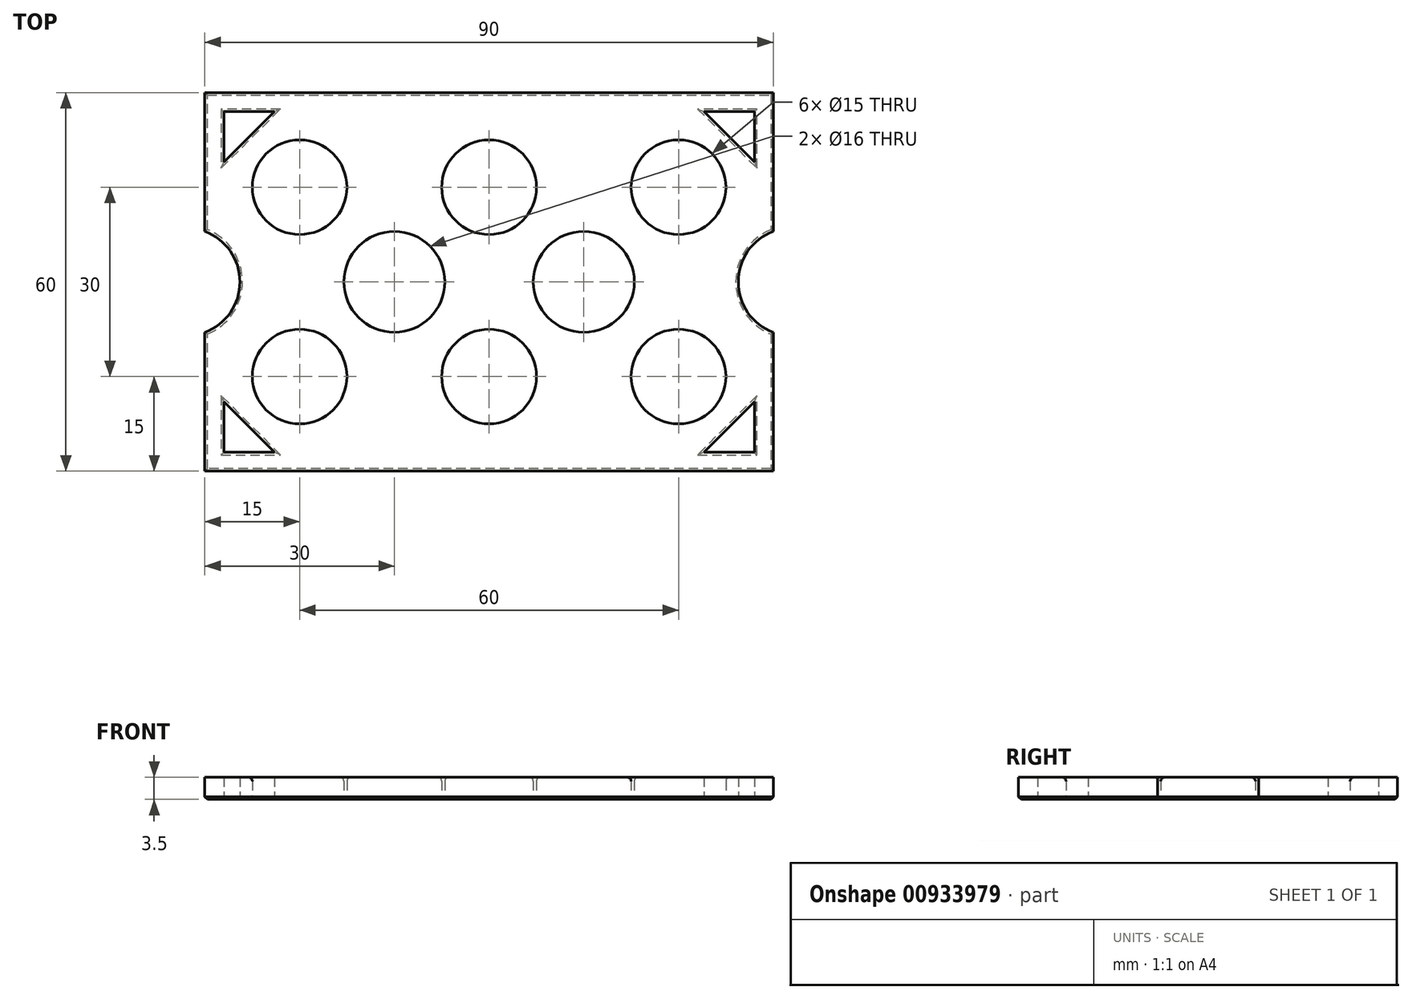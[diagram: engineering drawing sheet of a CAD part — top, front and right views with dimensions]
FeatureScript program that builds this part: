
annotation { "Feature Type Name" : "Feature", "Feature Type Description" : "" }
export const myFeature = defineFeature(function(context is Context, id is Id, definition is map)
    precondition{}
    {
        {
            var Q0;
            Q0=qCreatedBy(makeId("Top.planeOp"),FACE);
            var sketch = newSketch(context, id + "F0", { "sketchPlane" : qUnion([Q0])});
            skLineSegment(sketch, "E0.bottom", {"start": v(-45, 30) * mm, "end": v(45, 30) * mm});
            skLineSegment(sketch, "E0.top", {"start": v(-45, -30) * mm, "end": v(45, -30) * mm});
            skLineSegment(sketch, "E0.left", {"start": v(-45, 30) * mm, "end": v(-45, -30) * mm});
            skLineSegment(sketch, "E0.right", {"start": v(45, 30) * mm, "end": v(45, -30) * mm});
            skPoint(sketch, "E1", {"position": v(45, 0) * mm});
            skPoint(sketch, "E2", {"position": v(0, -30) * mm});
            skSolve(sketch);
        }
        {
            var Q0;
            Q0=qSketchRegion(id+"F0",true);
            extrude(context, id + "F1", {"entities" : qUnion([Q0]), "depth" : 3.5 * mm, "offsetDistance" : 25 * mm});
        }
        {
            var Q0;
            Q0=qCreatedBy(makeId("Top.planeOp"),FACE);
            var sketch = newSketch(context, id + "F2", { "sketchPlane" : qUnion([Q0])});
            skCircle(sketch, "E3", {"center": v(0, 15) * mm, "radius": 7.5 * mm});
            skCircle(sketch, "E4", {"center": v(30, 15) * mm, "radius": 7.5 * mm});
            skCircle(sketch, "E5", {"center": v(15, 0) * mm, "radius": 8 * mm});
            skCircle(sketch, "E6.MirrorC", {"center": v(-30, 15) * mm, "radius": 7.5 * mm});
            skCircle(sketch, "E7.MirrorC", {"center": v(30, -15) * mm, "radius": 7.5 * mm});
            skCircle(sketch, "E8.MirrorC", {"center": v(0, -15) * mm, "radius": 7.5 * mm});
            skCircle(sketch, "E9.MirrorC", {"center": v(-30, -15) * mm, "radius": 7.5 * mm});
            skCircle(sketch, "E10.MirrorC", {"center": v(-15, 0) * mm, "radius": 8 * mm});
            skSolve(sketch);
        }
        {
            var Q0;
            Q0=qSketchRegion(id+"F2",true);
            extrude(context, id + "F3", {"entities" : qUnion([Q0]), "operationType" : NewBodyOperationType.REMOVE, "endBound" : BoundingType.UP_TO_NEXT, "depth" : 25 * mm, "offsetDistance" : 25 * mm});
        }
        {
            var Q0;
            Q0=qCreatedBy(makeId("Top.planeOp"),FACE);
            var sketch = newSketch(context, id + "F4", { "sketchPlane" : qUnion([Q0])});
            skLineSegment(sketch, "E11.bottom", {"start": v(-42, 27) * mm, "end": v(-34, 27) * mm});
            skLineSegment(sketch, "E11.left", {"start": v(-42, 27) * mm, "end": v(-42, 19) * mm});
            skLineSegment(sketch, "E12", {"start": v(-42, 19) * mm, "end": v(-34, 27) * mm});
            skLineSegment(sketch, "E13.MirrorCS", {"start": v(42, 19) * mm, "end": v(34, 27) * mm});
            skLineSegment(sketch, "E14.MirrorCS", {"start": v(42, 27) * mm, "end": v(34, 27) * mm});
            skLineSegment(sketch, "E15.MirrorCS", {"start": v(42, 27) * mm, "end": v(42, 19) * mm});
            skLineSegment(sketch, "E16.MirrorCS", {"start": v(-42, -19) * mm, "end": v(-34, -27) * mm});
            skLineSegment(sketch, "E17.MirrorCS", {"start": v(-42, -27) * mm, "end": v(-42, -19) * mm});
            skLineSegment(sketch, "E18.MirrorCS", {"start": v(-42, -27) * mm, "end": v(-34, -27) * mm});
            skLineSegment(sketch, "E19.MirrorCS", {"start": v(42, -19) * mm, "end": v(34, -27) * mm});
            skLineSegment(sketch, "E20.MirrorCS", {"start": v(42, -27) * mm, "end": v(42, -19) * mm});
            skLineSegment(sketch, "E21.MirrorCS", {"start": v(42, -27) * mm, "end": v(34, -27) * mm});
            skSolve(sketch);
        }
        {
            var Q0;
            Q0 = qSketchRegion(id + "F4", true);
            extrude(context, id + "F5", {"entities" : qUnion([Q0]), "operationType" : NewBodyOperationType.REMOVE, "endBound" : BoundingType.UP_TO_NEXT, "depth" : 25 * mm, "offsetDistance" : 25 * mm});
        }
        {
            var Q0;
            Q0=qCreatedBy(makeId("Top.planeOp"),FACE);
            var sketch = newSketch(context, id + "F6", { "sketchPlane" : qUnion([Q0])});
            skPoint(sketch, "E22", {"position": v(-45, 8) * mm});
            skPoint(sketch, "E23", {"position": v(-45, -8) * mm});
            skArc(sketch, "E24", {"start": v(-45, -8) * mm, "mid": v(-39.46, 0) * mm, "end": v(-45, 8) * mm});
            skLineSegment(sketch, "E25", {"start": v(-45, 8) * mm, "end": v(-45, -8) * mm});
            skArc(sketch, "E26.MirrorCS", {"start": v(45, -8) * mm, "mid": v(39.46, 0) * mm, "end": v(45, 8) * mm});
            skLineSegment(sketch, "E27.MirrorCS", {"start": v(45, 8) * mm, "end": v(45, -8) * mm});
            skSolve(sketch);
        }
        {
            var Q0;
            Q0 = qSketchRegion(id + "F6", true);
            extrude(context, id + "F7", {"entities" : qUnion([Q0]), "operationType" : NewBodyOperationType.REMOVE, "endBound" : BoundingType.UP_TO_NEXT, "depth" : 25 * mm, "offsetDistance" : 25 * mm});
        }
        {
            var Q0;
            Q0=makeQuery(id+"F3.boolean.opBoolean","COPY",FACE,{"derivedFrom":makeQuery(id+"F3.opExtrude","SWEPT_FACE",FACE,{"disambiguationData":[OSD([sQuery(id+"F2.wireOp",EDGE,"E6.MirrorC")])]})});
            var Q1;
            Q1=makeQuery(id+"F3.boolean.opBoolean","COPY",FACE,{"derivedFrom":makeQuery(id+"F3.opExtrude","SWEPT_FACE",FACE,{"disambiguationData":[OSD([sQuery(id+"F2.wireOp",EDGE,"E3")])]})});
            var Q2;
            Q2=makeQuery(id+"F3.boolean.opBoolean","COPY",FACE,{"derivedFrom":makeQuery(id+"F3.opExtrude","SWEPT_FACE",FACE,{"disambiguationData":[OSD([sQuery(id+"F2.wireOp",EDGE,"E4")])]})});
            var Q3;
            Q3=makeQuery(id+"F3.boolean.opBoolean","COPY",FACE,{"derivedFrom":makeQuery(id+"F3.opExtrude","SWEPT_FACE",FACE,{"disambiguationData":[OSD([sQuery(id+"F2.wireOp",EDGE,"E5")])]})});
            var Q4;
            Q4=makeQuery(id+"F3.boolean.opBoolean","COPY",FACE,{"derivedFrom":makeQuery(id+"F3.opExtrude","SWEPT_FACE",FACE,{"disambiguationData":[OSD([sQuery(id+"F2.wireOp",EDGE,"E10.MirrorC")])]})});
            var Q5;
            Q5=makeQuery(id+"F3.boolean.opBoolean","COPY",FACE,{"derivedFrom":makeQuery(id+"F3.opExtrude","SWEPT_FACE",FACE,{"disambiguationData":[OSD([sQuery(id+"F2.wireOp",EDGE,"E9.MirrorC")])]})});
            var Q6;
            Q6=makeQuery(id+"F3.boolean.opBoolean","COPY",FACE,{"derivedFrom":makeQuery(id+"F3.opExtrude","SWEPT_FACE",FACE,{"disambiguationData":[OSD([sQuery(id+"F2.wireOp",EDGE,"E8.MirrorC")])]})});
            var Q7;
            Q7=makeQuery(id+"F3.boolean.opBoolean","COPY",FACE,{"derivedFrom":makeQuery(id+"F3.opExtrude","SWEPT_FACE",FACE,{"disambiguationData":[OSD([sQuery(id+"F2.wireOp",EDGE,"E7.MirrorC")])]})});
            fillet(context, id + "F8", {"entities" : qUnion([Q0, Q1, Q2, Q3, Q4, Q5, Q6, Q7]), "radius" : .6 * mm, "tangentPropagation" : true, "allowEdgeOverflow" : false});
        }
        {
            var Q0;
            Q0=makeQuery(id+"F1.opExtrude","CAP_FACE",FACE,{"disambiguationData":[OSD([sQuery(id+"F0.wireOp",EDGE,"E0.bottom"),sQuery(id+"F0.wireOp",EDGE,"E0.top"),sQuery(id+"F0.wireOp",EDGE,"E0.left"),sQuery(id+"F0.wireOp",EDGE,"E0.right")])],"isStart":true});
            var Q1;
            Q1=makeQuery(id+"F5.boolean.opBoolean","COPY",EDGE,{"derivedFrom":makeQuery(id+"F5.opExtrude","CAP_EDGE",EDGE,{"disambiguationData":[OSD([sQuery(id+"F4.wireOp",EDGE,"E16.MirrorCS")])],"isStart":false})});
            var Q2;
            Q2=makeQuery(id+"F5.boolean.opBoolean","COPY",EDGE,{"derivedFrom":makeQuery(id+"F5.opExtrude","CAP_EDGE",EDGE,{"disambiguationData":[OSD([sQuery(id+"F4.wireOp",EDGE,"E17.MirrorCS")])],"isStart":false})});
            var Q3;
            Q3=makeQuery(id+"F5.boolean.opBoolean","COPY",EDGE,{"derivedFrom":makeQuery(id+"F5.opExtrude","CAP_EDGE",EDGE,{"disambiguationData":[OSD([sQuery(id+"F4.wireOp",EDGE,"E18.MirrorCS")])],"isStart":false})});
            var Q4;
            Q4=makeQuery(id+"F5.boolean.opBoolean","COPY",EDGE,{"derivedFrom":makeQuery(id+"F5.opExtrude","CAP_EDGE",EDGE,{"disambiguationData":[OSD([sQuery(id+"F4.wireOp",EDGE,"E11.bottom")])],"isStart":false})});
            var Q5;
            Q5=makeQuery(id+"F5.boolean.opBoolean","COPY",EDGE,{"derivedFrom":makeQuery(id+"F5.opExtrude","CAP_EDGE",EDGE,{"disambiguationData":[OSD([sQuery(id+"F4.wireOp",EDGE,"E11.left")])],"isStart":false})});
            var Q6;
            Q6=makeQuery(id+"F5.boolean.opBoolean","COPY",EDGE,{"derivedFrom":makeQuery(id+"F5.opExtrude","CAP_EDGE",EDGE,{"disambiguationData":[OSD([sQuery(id+"F4.wireOp",EDGE,"E12")])],"isStart":false})});
            var Q7;
            Q7=makeQuery(id+"F5.boolean.opBoolean","COPY",EDGE,{"derivedFrom":makeQuery(id+"F5.opExtrude","CAP_EDGE",EDGE,{"disambiguationData":[OSD([sQuery(id+"F4.wireOp",EDGE,"E14.MirrorCS")])],"isStart":false})});
            var Q8;
            Q8=makeQuery(id+"F5.boolean.opBoolean","COPY",EDGE,{"derivedFrom":makeQuery(id+"F5.opExtrude","CAP_EDGE",EDGE,{"disambiguationData":[OSD([sQuery(id+"F4.wireOp",EDGE,"E13.MirrorCS")])],"isStart":false})});
            var Q9;
            Q9=makeQuery(id+"F5.boolean.opBoolean","COPY",EDGE,{"derivedFrom":makeQuery(id+"F5.opExtrude","CAP_EDGE",EDGE,{"disambiguationData":[OSD([sQuery(id+"F4.wireOp",EDGE,"E15.MirrorCS")])],"isStart":false})});
            var Q10;
            Q10=makeQuery(id+"F5.boolean.opBoolean","COPY",EDGE,{"derivedFrom":makeQuery(id+"F5.opExtrude","CAP_EDGE",EDGE,{"disambiguationData":[OSD([sQuery(id+"F4.wireOp",EDGE,"E20.MirrorCS")])],"isStart":false})});
            var Q11;
            Q11=makeQuery(id+"F5.boolean.opBoolean","COPY",EDGE,{"derivedFrom":makeQuery(id+"F5.opExtrude","CAP_EDGE",EDGE,{"disambiguationData":[OSD([sQuery(id+"F4.wireOp",EDGE,"E19.MirrorCS")])],"isStart":false})});
            var Q12;
            Q12=makeQuery(id+"F5.boolean.opBoolean","COPY",EDGE,{"derivedFrom":makeQuery(id+"F5.opExtrude","CAP_EDGE",EDGE,{"disambiguationData":[OSD([sQuery(id+"F4.wireOp",EDGE,"E21.MirrorCS")])],"isStart":false})});
            chamfer(context, id + "F9", {"entities" : qUnion([Q0, Q1, Q2, Q3, Q4, Q5, Q6, Q7, Q8, Q9, Q10, Q11, Q12]), "width" : .4 * mm, "tangentPropagation" : true});
        }
    });
